# Revit family: Haworth_BuzziBlinds_Screen_Beach
name_source: partatom
category: Furniture
revit_build: Autodesk Revit 2018 (Build: 20170223_1515(x64)
units: mm (PartAtom-declared; Revit-internal decimal feet)

## family parameters
Always vertical = Yes
Cut with Voids When Loaded = No
OmniClass Number = 23.40.20.00
OmniClass Title = General Furniture and Specialties
Room Calculation Point = No
Shared = No
Work Plane-Based = No

## types (8) — shared parameters
Actual Depth = 19.29 "
Actual Width = 58.66 "
Assembly Code = E2020200
Manufacturer = Haworth
Model = HCBZ-BD
Revision = 1
Screen Spacing = 11.811 "
Size = Verify Final Dim. w/ Haworth
URL = http://www.haworth.com
URL - Product = https://www.haworth.com
Warranty = http://www.haworth.com

## per-type parameters (varying)
| type | Actual Height | Casters | Description | Large | Medium | With Lines |
| HCBZ-BDB3-CFL - Large Screen - With Lines - With Casters | 72.83 " | Yes | Haworth BuzziBlinds - Beach Large Screen - With Lines - With Casters | Yes | No | Yes |
| HCBZ-BDB3-NFL - Large Screen - With Lines - Without Casters | 72.83 " | No | Haworth BuzziBlinds - Beach Large Screen - With Lines - Without Casters | Yes | No | Yes |
| HCBZ-BDB3-CF - Large Screen - Without Lines - With Casters | 72.83 " | Yes | Haworth BuzziBlinds - Beach Large Screen - Without Lines - With Casters | Yes | No | No |
| HCBZ-BDB3-N - Large Screen - Without Lines - Without Casters | 72.83 " | No | Haworth BuzziBlinds - Beach Large Screen - Without Lines - Without Casters | Yes | No | No |
| HCBZ-BDB2-N - Medium Screen - Without Lines - Without Casters | 59.06 " | No | Haworth BuzziBlinds - Beach Medium Screen - Without Lines - Without Casters | No | Yes | No |
| HCBZ-BDB2-CFL - Medium Screen - With Lines - With Casters | 59.06 " | Yes | Haworth BuzziBlinds - Beach Medium Screen - With Lines - With Casters | No | Yes | Yes |
| HCBZ-BDB2-CF - Medium Screen - Without Lines - With Casters | 59.06 " | Yes | Haworth BuzziBlinds - Beach Medium Screen - Without Lines - With Casters | No | Yes | No |
| HCBZ-BDB2-NFL - Medium Screen - With Lines - Without Casters | 59.06 " | No | Haworth BuzziBlinds - Beach Medium Screen - With Lines - Without Casters | No | Yes | Yes |

## geometry (parser evidence)
native form markers: Sweep x16
no freeform markers — native parametric forms only
